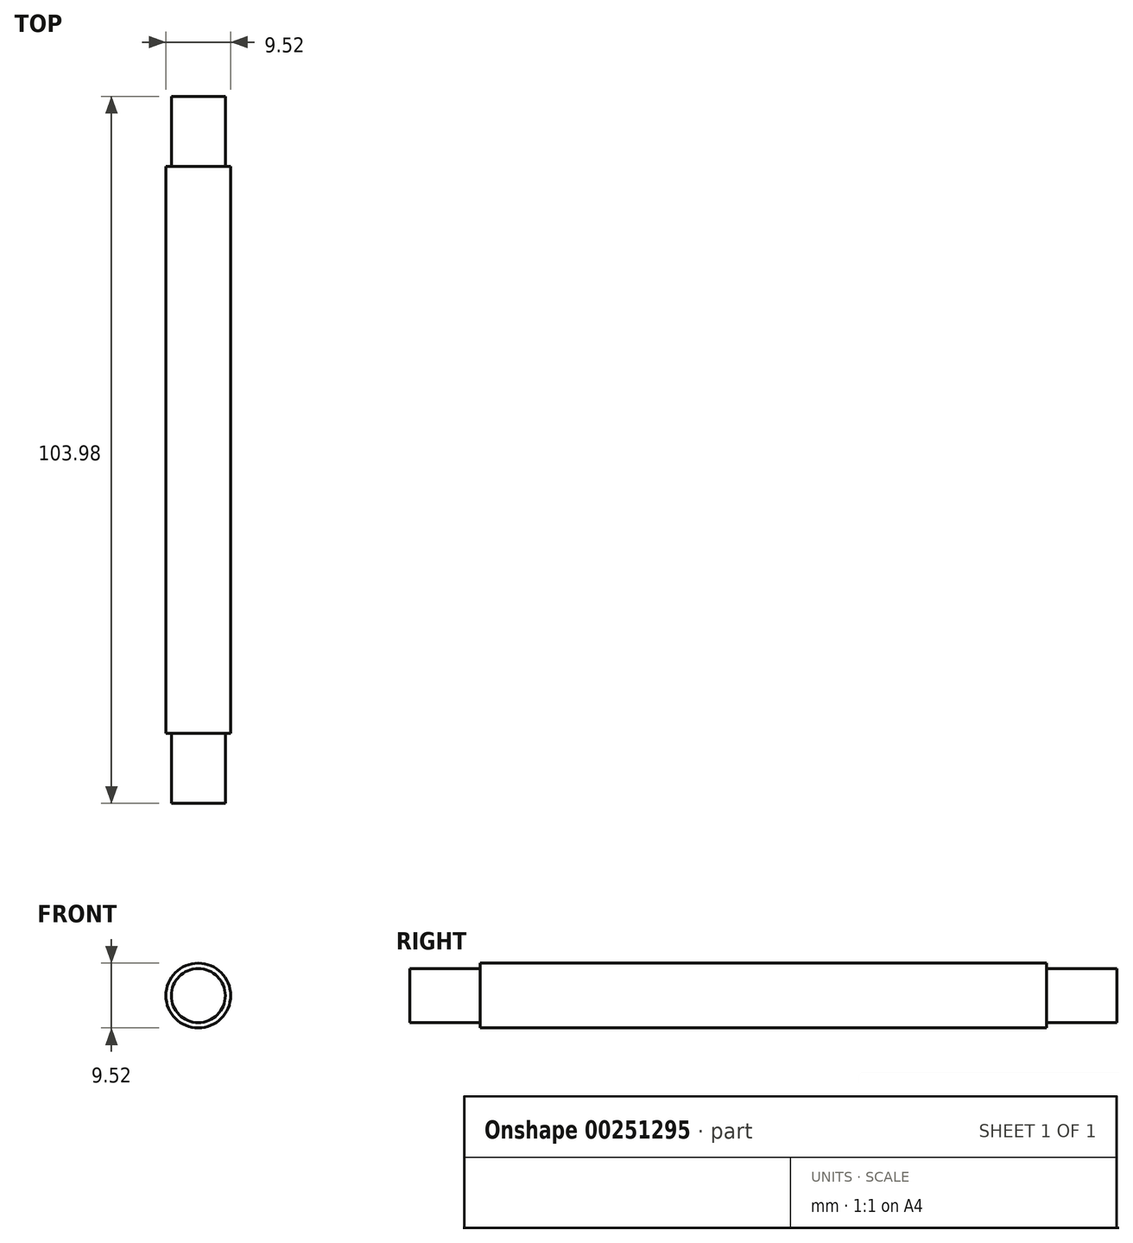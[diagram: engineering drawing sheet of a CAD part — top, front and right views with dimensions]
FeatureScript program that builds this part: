
annotation { "Feature Type Name" : "Feature", "Feature Type Description" : "" }
export const myFeature = defineFeature(function(context is Context, id is Id, definition is map)
    precondition{}
    {
        {
            var Q0;
            Q0=qCreatedBy(makeId("Front.planeOp"),FACE);
            var sketch = newSketch(context, id + "F0", { "sketchPlane" : qUnion([Q0])});
            skCircle(sketch, "E0", {"center": v(0, 0) * mm, "radius": 4.76 * mm});
            skSolve(sketch);
        }
        {
            var Q0;
            Q0 = qSketchRegion(id + "F0", true);
            extrude(context, id + "F1", {"entities" : qUnion([Q0]), "depth" : 83.34 * mm});
        }
        {
            var Q0;
            Q0=makeQuery(id+"F1.opExtrude","CAP_FACE",FACE,{"disambiguationData":[OSD([sQuery(id+"F0.wireOp",EDGE,"E0")])],"isStart":false});
            var sketch = newSketch(context, id + "F2", { "sketchPlane" : qUnion([Q0])});
            skCircle(sketch, "E1", {"center": v(0, 0) * mm, "radius": 3.97 * mm});
            skSolve(sketch);
        }
        {
            var Q0;
            Q0=makeQuery(id+"F2.imprint","IMPRINT",FACE,{"disambiguationData":[TD([[makeQuery(id+"F2.imprint","IMPRINT",EDGE,{"derivedFrom":sQuery(id+"F2.wireOp",EDGE,"E1")}),1.0]])]});
            extrude(context, id + "F3", {"entities" : qUnion([Q0]), "operationType" : NewBodyOperationType.ADD, "depth" : 10.32 * mm});
        }
        {
            var Q0;
            Q0=makeQuery(id+"F1.opExtrude","CAP_FACE",FACE,{"disambiguationData":[OSD([sQuery(id+"F0.wireOp",EDGE,"E0")])],"isStart":true});
            var sketch = newSketch(context, id + "F4", { "sketchPlane" : qUnion([Q0])});
            skCircle(sketch, "E2", {"center": v(0, 0) * mm, "radius": 3.97 * mm});
            skSolve(sketch);
        }
        {
            var Q0;
            Q0 = qSketchRegion(id + "F4", true);
            extrude(context, id + "F5", {"entities" : qUnion([Q0]), "operationType" : NewBodyOperationType.ADD, "depth" : 10.32 * mm});
        }
    });
